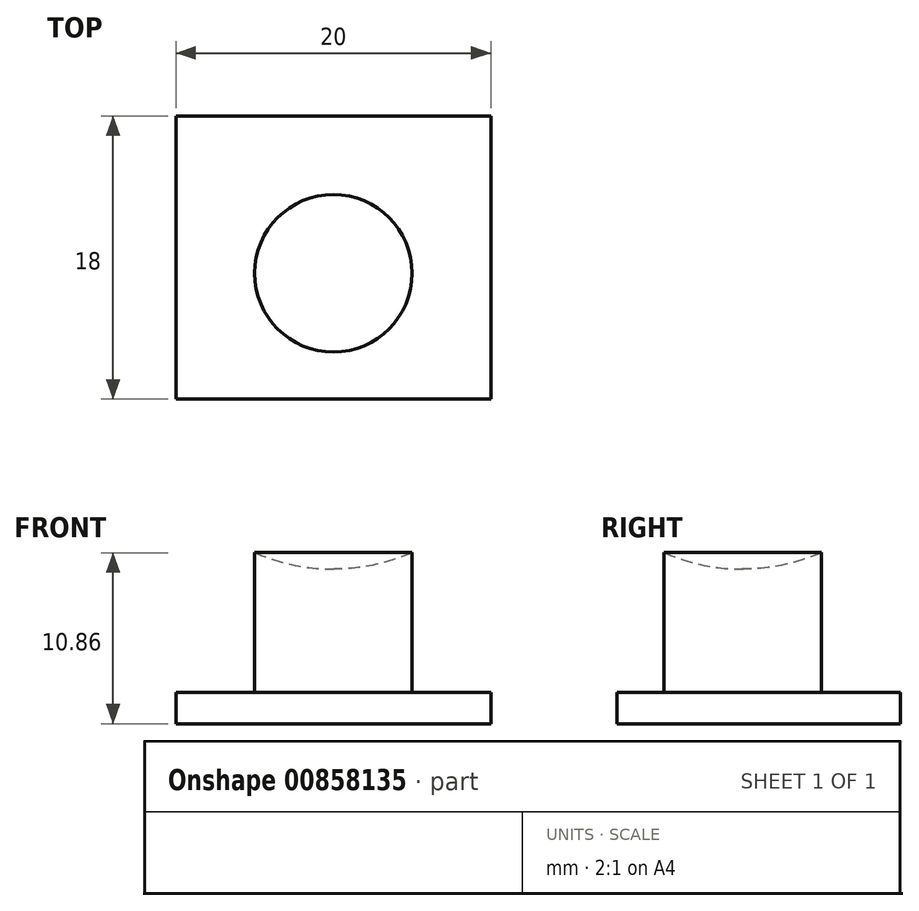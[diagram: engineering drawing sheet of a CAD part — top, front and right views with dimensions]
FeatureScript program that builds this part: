
annotation { "Feature Type Name" : "Feature", "Feature Type Description" : "" }
export const myFeature = defineFeature(function(context is Context, id is Id, definition is map)
    precondition{}
    {
        {
            var Q0;
            Q0=qCreatedBy(makeId("Top.planeOp"),FACE);
            var sketch = newSketch(context, id + "F0", { "sketchPlane" : qUnion([Q0])});
            skLineSegment(sketch, "E0.bottom", {"start": v(10, -10) * mm, "end": v(-10, -10) * mm});
            skLineSegment(sketch, "E0.top", {"start": v(10, 10) * mm, "end": v(-10, 10) * mm});
            skLineSegment(sketch, "E0.left", {"start": v(10, -10) * mm, "end": v(10, 10) * mm});
            skLineSegment(sketch, "E0.right", {"start": v(-10, -10) * mm, "end": v(-10, 10) * mm});
            skPoint(sketch, "E0.middle", {"position": v(0, 0) * mm});
            skCircle(sketch, "E1", {"center": v(0, 0) * mm, "radius": 5 * mm});
            skSolve(sketch);
        }
        {
            var Q0;
            Q0 = qSketchRegion(id + "F0", true);
            var Q1;
            Q1=makeQuery(id+"F0.imprint","IMPRINT",FACE,{"disambiguationData":[TD([[makeQuery(id+"F0.imprint","IMPRINT",EDGE,{"derivedFrom":sQuery(id+"F0.wireOp",EDGE,"E1")}),1.0]])]});
            extrude(context, id + "F1", {"entities" : qUnion([Q0, Q1]), "oppositeDirection" : true, "depth" : 2 * mm, "offsetDistance" : 25 * mm});
        }
        {
            var Q0;
            Q0=makeQuery(id+"F0.imprint","IMPRINT",FACE,{"disambiguationData":[TD([[makeQuery(id+"F0.imprint","IMPRINT",EDGE,{"derivedFrom":sQuery(id+"F0.wireOp",EDGE,"E1")}),1.0]])]});
            extrude(context, id + "F2", {"entities" : qUnion([Q0]), "operationType" : NewBodyOperationType.ADD, "depth" : 10 * mm, "offsetDistance" : 25 * mm});
        }
        {
            var Q0;
            Q0=qCreatedBy(makeId("Right.planeOp"),FACE);
            var sketch = newSketch(context, id + "F3", { "sketchPlane" : qUnion([Q0])});
            skLineSegment(sketch, "E2", {"start": v(0, 0) * mm, "end": v(0, 32.42) * mm});
            skArc(sketch, "E3", {"start": v(0, 7.82) * mm, "mid": v(12.34, 20.12) * mm, "end": v(0, 32.42) * mm});
            skSolve(sketch);
        }
        {
            var Q0;
            {var subQ0=sQuery(id+"F3.wireOp",EDGE,"E3");Q0=makeQuery(id+"F3.imprint","IMPRINT",FACE,{"disambiguationData":[TD([[makeQuery(id+"F3.imprint","IMPRINT",EDGE,{"derivedFrom":subQ0}),1.0]])]});}
            var Q1;
            Q1=sQuery(id+"F3.wireOp",EDGE,"E2");
            revolve(context, id + "F4", {"operationType" : NewBodyOperationType.ADD, "surfaceOperationType" : NewSurfaceOperationType.NEW, "entities" : qUnion([Q0]), "axis" : qUnion([Q1]), "revolveType" : RevolveType.FULL});
        }
        {
            var Q0;
            Q0=makeQuery(id+"F1.opExtrude","SWEPT_FACE",FACE,{"disambiguationData":[OSD([sQuery(id+"F0.wireOp",EDGE,"E0.bottom")])]});
            var sketch = newSketch(context, id + "F5", { "sketchPlane" : qUnion([Q0])});
            skLineSegment(sketch, "E4.bottom", {"start": v(-10, -2) * mm, "end": v(10, -2) * mm});
            skLineSegment(sketch, "E4.top", {"start": v(-10, 48) * mm, "end": v(10, 48) * mm});
            skLineSegment(sketch, "E4.left", {"start": v(-10, -2) * mm, "end": v(-10, 48) * mm});
            skLineSegment(sketch, "E4.right", {"start": v(10, -2) * mm, "end": v(10, 48) * mm});
            skSolve(sketch);
        }
        {
            var Q0;
            {var subQ0=sQuery(id+"F5.wireOp",EDGE,"E4.top");Q0=makeQuery(id+"F5.imprint","IMPRINT",FACE,{"disambiguationData":[TD([[makeQuery(id+"F5.imprint","IMPRINT",EDGE,{"derivedFrom":subQ0}),-1.0]])]});}
            extrude(context, id + "F6", {"entities" : qUnion([Q0]), "operationType" : NewBodyOperationType.REMOVE, "oppositeDirection" : true, "depth" : 2 * mm, "offsetDistance" : 25 * mm});
        }
        {
            var Q0;
            Q0 = qSketchRegion(id + "F5", true);
            extrude(context, id + "F7", {"entities" : qUnion([Q0]), "operationType" : NewBodyOperationType.REMOVE, "depth" : 5 * mm, "offsetDistance" : 25 * mm});
        }
        {
            var Q0;
            Q0 = qSketchRegion(id + "F5", true);
            extrude(context, id + "F8", {"entities" : qUnion([Q0]), "operationType" : NewBodyOperationType.REMOVE, "oppositeDirection" : true, "depth" : 2 * mm, "offsetDistance" : 25 * mm});
        }
    });
